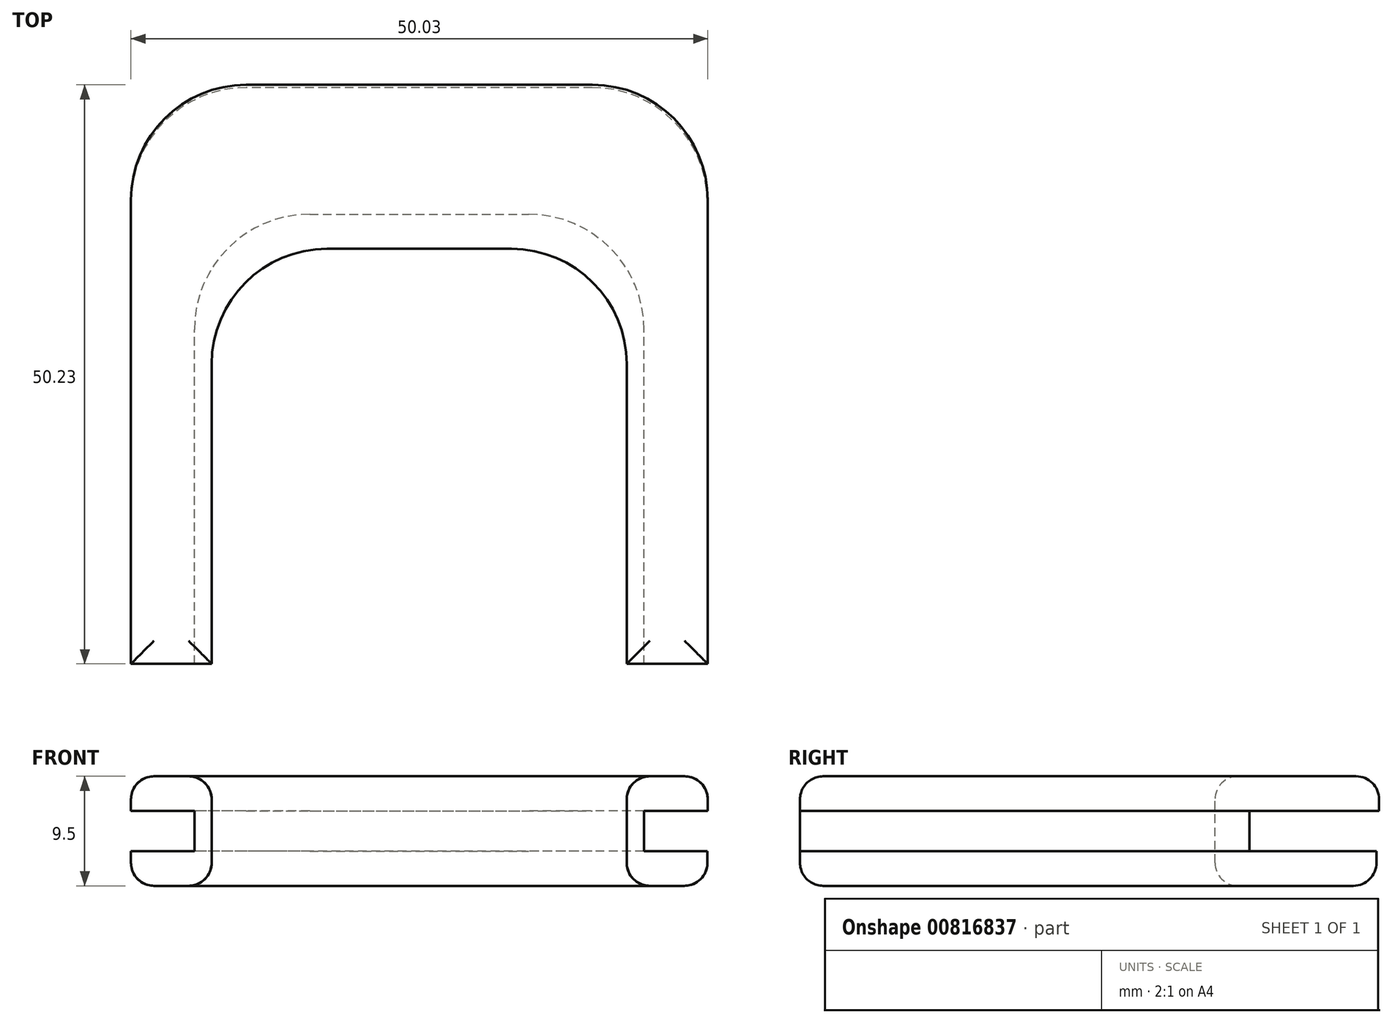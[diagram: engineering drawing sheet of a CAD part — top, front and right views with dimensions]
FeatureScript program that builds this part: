
annotation { "Feature Type Name" : "Feature", "Feature Type Description" : "" }
export const myFeature = defineFeature(function(context is Context, id is Id, definition is map)
    precondition{}
    {
        {
            var Q0;
            Q0=qCreatedBy(makeId("Top.planeOp"),FACE);
            var sketch = newSketch(context, id + "F0", { "sketchPlane" : qUnion([Q0])});
            skLineSegment(sketch, "E0.bottom", {"start": v(25, -25) * mm, "end": v(-25, -25) * mm});
            skLineSegment(sketch, "E0.top", {"start": v(25, 25) * mm, "end": v(-25, 25) * mm});
            skLineSegment(sketch, "E0.left", {"start": v(25, -25) * mm, "end": v(25, 25) * mm});
            skLineSegment(sketch, "E0.right", {"start": v(-25, -25) * mm, "end": v(-25, 25) * mm});
            skPoint(sketch, "E0.middle", {"position": v(0, 0) * mm});
            skPoint(sketch, "E1.visualSharp", {"position": v(-25, 25) * mm});
            skLineSegment(sketch, "E1.filletArc", {"start": v(-25, 25) * mm, "end": v(-25, 25) * mm});
            skPoint(sketch, "E2.visualSharp", {"position": v(25, 25) * mm});
            skLineSegment(sketch, "E2.filletArc", {"start": v(25, 25) * mm, "end": v(25, 25) * mm});
            skSolve(sketch);
        }
        {
            var Q0;
            Q0=qSketchRegion(id+"F0",true);
            extrude(context, id + "F1", {"entities" : qUnion([Q0]), "depth" : 3 * mm, "offsetDistance" : 25 * mm});
        }
        {
            var Q0;
            Q0=makeQuery(id+"F1.opExtrude","CAP_FACE",FACE,{"disambiguationData":[OSD([sQuery(id+"F0.wireOp",EDGE,"E0.bottom"),sQuery(id+"F0.wireOp",EDGE,"E0.top"),sQuery(id+"F0.wireOp",EDGE,"E0.left"),sQuery(id+"F0.wireOp",EDGE,"E0.right"),sQuery(id+"F0.wireOp",EDGE,"E1.filletArc"),sQuery(id+"F0.wireOp",EDGE,"E2.filletArc")])],"isStart":false});
            var sketch = newSketch(context, id + "F2", { "sketchPlane" : qUnion([Q0])});
            skLineSegment(sketch, "E3.bottom", {"start": v(-19.5, -25) * mm, "end": v(19.5, -25) * mm});
            skLineSegment(sketch, "E3.top", {"start": v(-19.5, 14) * mm, "end": v(19.5, 14) * mm});
            skLineSegment(sketch, "E3.left", {"start": v(-19.5, -25) * mm, "end": v(-19.5, 14) * mm});
            skLineSegment(sketch, "E3.right", {"start": v(19.5, -25) * mm, "end": v(19.5, 14) * mm});
            skLineSegment(sketch, "E4", {"start": v(0, 25) * mm, "end": v(0, -25) * mm, "construction": true});
            skPoint(sketch, "E5.visualSharp", {"position": v(-19.5, 14) * mm});
            skLineSegment(sketch, "E5.filletArc", {"start": v(-19.5, 14) * mm, "end": v(-19.5, 14) * mm});
            skPoint(sketch, "E6.visualSharp", {"position": v(19.5, 14) * mm});
            skLineSegment(sketch, "E6.filletArc", {"start": v(19.5, 14) * mm, "end": v(19.5, 14) * mm});
            skSolve(sketch);
        }
        {
            var Q0;
            Q0=qSketchRegion(id+"F2",true);
            extrude(context, id + "F3", {"entities" : qUnion([Q0]), "operationType" : NewBodyOperationType.ADD, "depth" : 3.5 * mm, "offsetDistance" : 25 * mm});
        }
        {
            var Q0;
            Q0=makeQuery(id+"F3.opExtrude","CAP_FACE",FACE,{"disambiguationData":[OSD([sQuery(id+"F2.wireOp",EDGE,"E3.bottom"),sQuery(id+"F2.wireOp",EDGE,"E3.top"),sQuery(id+"F2.wireOp",EDGE,"E3.left"),sQuery(id+"F2.wireOp",EDGE,"E3.right"),sQuery(id+"F2.wireOp",EDGE,"E5.filletArc"),sQuery(id+"F2.wireOp",EDGE,"E6.filletArc")])],"isStart":false});
            var sketch = newSketch(context, id + "F4", { "sketchPlane" : qUnion([Q0])});
            skLineSegment(sketch, "E7.bottom", {"start": v(-18, -25) * mm, "end": v(18, -25) * mm});
            skLineSegment(sketch, "E7.top", {"start": v(-18, 11) * mm, "end": v(18, 11) * mm});
            skLineSegment(sketch, "E7.left", {"start": v(-18, -25) * mm, "end": v(-18, 11) * mm});
            skLineSegment(sketch, "E7.right", {"start": v(18, -25) * mm, "end": v(18, 11) * mm});
            skLineSegment(sketch, "E8", {"start": v(0, 25.07) * mm, "end": v(0, -25) * mm});
            skPoint(sketch, "E9.visualSharp", {"position": v(-18, 11) * mm});
            skLineSegment(sketch, "E9.filletArc", {"start": v(-18, 11) * mm, "end": v(-18, 11) * mm});
            skPoint(sketch, "E10.visualSharp", {"position": v(18, 11) * mm});
            skLineSegment(sketch, "E10.filletArc", {"start": v(18, 11) * mm, "end": v(18, 11) * mm});
            skSolve(sketch);
        }
        {
            var Q0;
            Q0=makeQuery(id+"F3.opExtrude","CAP_FACE",FACE,{"disambiguationData":[OSD([sQuery(id+"F2.wireOp",EDGE,"E3.bottom"),sQuery(id+"F2.wireOp",EDGE,"E3.top"),sQuery(id+"F2.wireOp",EDGE,"E3.left"),sQuery(id+"F2.wireOp",EDGE,"E3.right"),sQuery(id+"F2.wireOp",EDGE,"E5.filletArc"),sQuery(id+"F2.wireOp",EDGE,"E6.filletArc")])],"isStart":false});
            var sketch = newSketch(context, id + "F5", { "sketchPlane" : qUnion([Q0])});
            skLineSegment(sketch, "E11.0", {"start": v(-19.5, -25) * mm, "end": v(-25, -25) * mm});
            skLineSegment(sketch, "E12.0", {"start": v(25, 25) * mm, "end": v(25, 25) * mm});
            skLineSegment(sketch, "E13.bottom", {"start": v(-25, -25) * mm, "end": v(25.03, -25) * mm});
            skLineSegment(sketch, "E13.top", {"start": v(-25, 25.23) * mm, "end": v(25.03, 25.23) * mm});
            skLineSegment(sketch, "E13.left", {"start": v(-25, -25) * mm, "end": v(-25, 25.23) * mm});
            skLineSegment(sketch, "E13.right", {"start": v(25.03, -25) * mm, "end": v(25.03, 25.23) * mm});
            skSolve(sketch);
        }
        {
            var Q0;
            Q0=qSketchRegion(id+"F5",true);
            extrude(context, id + "F6", {"entities" : qUnion([Q0]), "operationType" : NewBodyOperationType.ADD, "depth" : 3 * mm, "offsetDistance" : 25 * mm});
        }
        {
            var Q0;
            Q0=makeQuery(id+"F1.opExtrude","SWEPT_EDGE",EDGE,{"disambiguationData":[OSD([sQuery(id+"F0.wireOp",EDGE,"E0.top"),sQuery(id+"F0.wireOp",EDGE,"E0.right")])]});
            var Q1;
            Q1=makeQuery(id+"F6.opExtrude","SWEPT_EDGE",EDGE,{"disambiguationData":[OSD([sQuery(id+"F5.wireOp",EDGE,"E13.top"),sQuery(id+"F5.wireOp",EDGE,"E13.left")])]});
            var Q2;
            Q2=makeQuery(id+"F6.opExtrude","SWEPT_EDGE",EDGE,{"disambiguationData":[OSD([sQuery(id+"F5.wireOp",EDGE,"E13.top"),sQuery(id+"F5.wireOp",EDGE,"E13.right")])]});
            var Q3;
            Q3=makeQuery(id+"F1.opExtrude","SWEPT_EDGE",EDGE,{"disambiguationData":[OSD([sQuery(id+"F0.wireOp",EDGE,"E0.top"),sQuery(id+"F0.wireOp",EDGE,"E0.left")])]});
            var Q4;
            Q4=makeQuery(id+"F3.opExtrude","SWEPT_EDGE",EDGE,{"disambiguationData":[OSD([sQuery(id+"F2.wireOp",EDGE,"E3.top"),sQuery(id+"F2.wireOp",EDGE,"E3.left")])]});
            var Q5;
            Q5=makeQuery(id+"F3.opExtrude","SWEPT_EDGE",EDGE,{"disambiguationData":[OSD([sQuery(id+"F2.wireOp",EDGE,"E3.top"),sQuery(id+"F2.wireOp",EDGE,"E3.right")])]});
            fillet(context, id + "F7", {"entities" : qUnion([Q0, Q1, Q2, Q3, Q4, Q5]), "radius" : 10 * mm, "tangentPropagation" : true, "allowEdgeOverflow" : false});
        }
        {
            var Q0;
            Q0=makeQuery(id+"F6.opExtrude","CAP_FACE",FACE,{"disambiguationData":[OSD([sQuery(id+"F5.wireOp",EDGE,"E13.bottom"),sQuery(id+"F5.wireOp",EDGE,"E13.top"),sQuery(id+"F5.wireOp",EDGE,"E13.left"),sQuery(id+"F5.wireOp",EDGE,"E13.right")])],"isStart":false});
            var sketch = newSketch(context, id + "F8", { "sketchPlane" : qUnion([Q0])});
            skLineSegment(sketch, "E14.bottom", {"start": v(-18, -25) * mm, "end": v(18, -25) * mm});
            skLineSegment(sketch, "E14.top", {"start": v(-8, 11) * mm, "end": v(8, 11) * mm});
            skLineSegment(sketch, "E14.left", {"start": v(-18, -25) * mm, "end": v(-18, 1) * mm});
            skLineSegment(sketch, "E14.right", {"start": v(18, -25) * mm, "end": v(18, 1) * mm});
            skLineSegment(sketch, "E15", {"start": v(0, 25.23) * mm, "end": v(0, -25) * mm, "construction": true});
            skPoint(sketch, "E16.visualSharp", {"position": v(-18, 11) * mm});
            skArc(sketch, "E16.filletArc", {"start": v(-8, 11) * mm, "mid": v(-15.07, 8.07) * mm, "end": v(-18, 1) * mm});
            skPoint(sketch, "E17.visualSharp", {"position": v(18, 11) * mm});
            skArc(sketch, "E17.filletArc", {"start": v(18, 1) * mm, "mid": v(15.07, 8.07) * mm, "end": v(8, 11) * mm});
            skSolve(sketch);
        }
        {
            var Q0;
            Q0=qSketchRegion(id+"F8",true);
            var Q1;
            Q1=makeQuery(id+"F1.opExtrude","CAP_FACE",FACE,{"disambiguationData":[OSD([sQuery(id+"F0.wireOp",EDGE,"E0.bottom"),sQuery(id+"F0.wireOp",EDGE,"E0.top"),sQuery(id+"F0.wireOp",EDGE,"E0.left"),sQuery(id+"F0.wireOp",EDGE,"E0.right")])],"isStart":true});
            extrude(context, id + "F9", {"entities" : qUnion([Q0]), "operationType" : NewBodyOperationType.REMOVE, "endBound" : BoundingType.UP_TO_SURFACE, "oppositeDirection" : true, "depth" : 25 * mm, "endBoundEntityFace" : qUnion([Q1]), "offsetDistance" : 25 * mm});
        }
        {
            var Q0;
            Q0=makeQuery(id+"F6.opExtrude","CAP_FACE",FACE,{"disambiguationData":[OSD([sQuery(id+"F5.wireOp",EDGE,"E13.bottom"),sQuery(id+"F5.wireOp",EDGE,"E13.top"),sQuery(id+"F5.wireOp",EDGE,"E13.left"),sQuery(id+"F5.wireOp",EDGE,"E13.right")])],"isStart":false});
            var Q1;
            Q1=makeQuery(id+"F1.opExtrude","CAP_FACE",FACE,{"disambiguationData":[OSD([sQuery(id+"F0.wireOp",EDGE,"E0.bottom"),sQuery(id+"F0.wireOp",EDGE,"E0.top"),sQuery(id+"F0.wireOp",EDGE,"E0.left"),sQuery(id+"F0.wireOp",EDGE,"E0.right")])],"isStart":true});
            fillet(context, id + "F10", {"entities" : qUnion([Q0, Q1]), "radius" : 2 * mm, "tangentPropagation" : true, "allowEdgeOverflow" : false});
        }
    });
